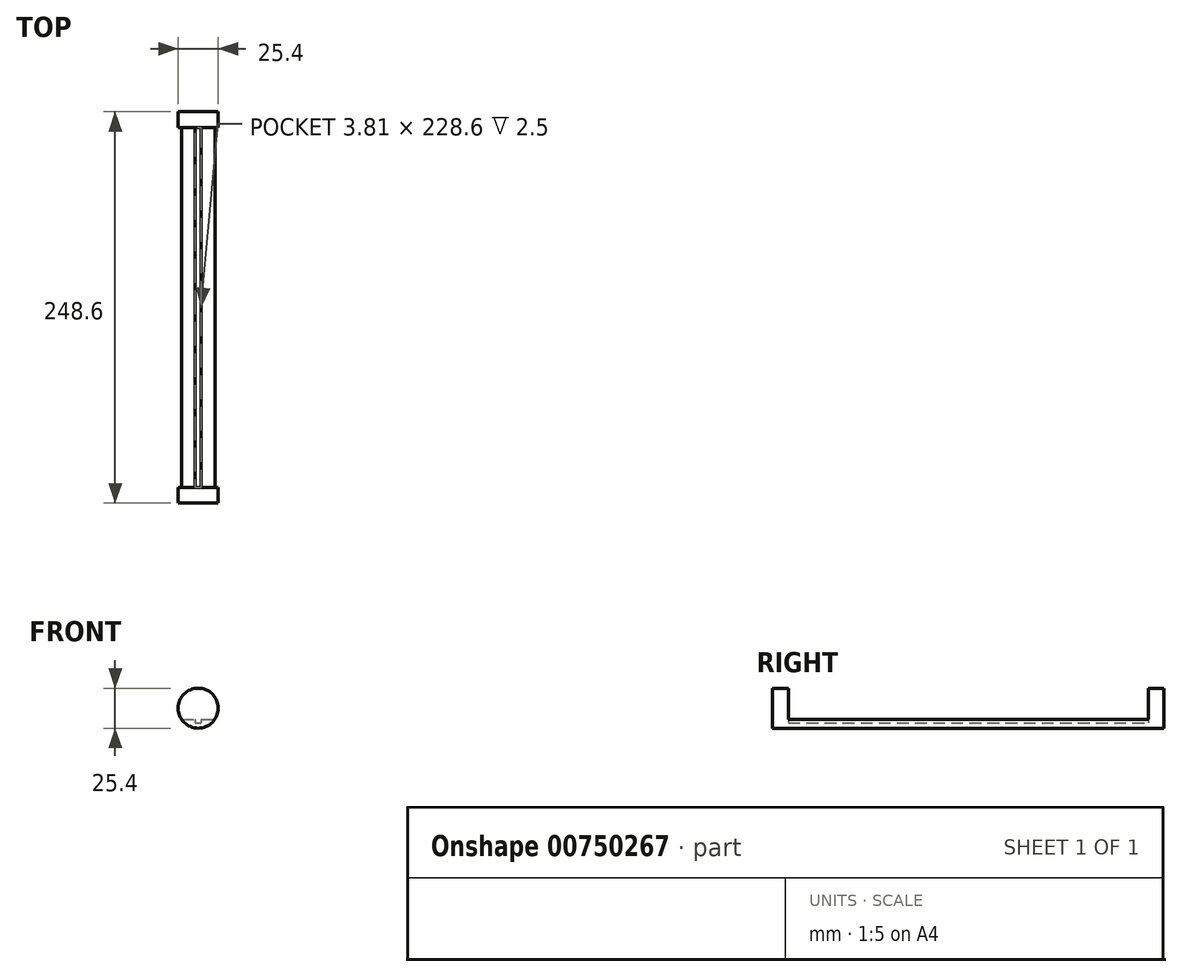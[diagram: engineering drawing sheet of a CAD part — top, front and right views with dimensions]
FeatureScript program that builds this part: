
annotation { "Feature Type Name" : "Feature", "Feature Type Description" : "" }
export const myFeature = defineFeature(function(context is Context, id is Id, definition is map)
    precondition{}
    {
        {
            var Q0;
            Q0=qCreatedBy(makeId("Front.planeOp"),FACE);
            var sketch = newSketch(context, id + "F0", { "sketchPlane" : qUnion([Q0])});
            skArc(sketch, "E0", {"start": v(-10.6, -7) * mm, "mid": v(0, -12.7) * mm, "end": v(10.6, -7) * mm});
            skLineSegment(sketch, "E1", {"start": v(-10.6, -7) * mm, "end": v(10.6, -7) * mm});
            skSolve(sketch);
        }
        {
            var Q0;
            Q0=qSketchRegion(id+"F0",true);
            extrude(context, id + "F1", {"entities" : qUnion([Q0]), "depth" : 114.3 * mm, "offsetDistance" : 25.4 * mm});
        }
        {
            var Q0;
            Q0=makeQuery(id+"F1.opExtrude","CAP_FACE",FACE,{"disambiguationData":[OSD([sQuery(id+"F0.wireOp",EDGE,"E0"),sQuery(id+"F0.wireOp",EDGE,"E1")])],"isStart":false});
            var sketch = newSketch(context, id + "F2", { "sketchPlane" : qUnion([Q0])});
            skCircle(sketch, "E2", {"center": v(0, 0) * mm, "radius": 12.7 * mm});
            skSolve(sketch);
        }
        {
            var Q0;
            Q0=qSketchRegion(id+"F2",true);
            extrude(context, id + "F3", {"entities" : qUnion([Q0]), "operationType" : NewBodyOperationType.ADD, "depth" : 10 * mm, "offsetDistance" : 25.4 * mm});
        }
        {
            var Q0;
            Q0=makeQuery(id+"F1.opExtrude","CAP_FACE",FACE,{"disambiguationData":[OSD([sQuery(id+"F0.wireOp",EDGE,"E0"),sQuery(id+"F0.wireOp",EDGE,"E1")])],"isStart":true});
            var sketch = newSketch(context, id + "F4", { "sketchPlane" : qUnion([Q0])});
            skArc(sketch, "E3", {"start": v(-10.6, -7) * mm, "mid": v(0, -12.7) * mm, "end": v(10.6, -7) * mm});
            skLineSegment(sketch, "E4", {"start": v(-10.6, -7) * mm, "end": v(10.6, -7) * mm});
            skLineSegment(sketch, "E5.top", {"start": v(1.9, -9.5) * mm, "end": v(-1.9, -9.5) * mm});
            skLineSegment(sketch, "E5.left", {"start": v(1.9, -7) * mm, "end": v(1.9, -9.5) * mm});
            skLineSegment(sketch, "E5.right", {"start": v(-1.9, -7) * mm, "end": v(-1.9, -9.5) * mm});
            skSolve(sketch);
        }
        {
            var Q0;
            Q0=makeQuery(id+"F4.imprint","IMPRINT",FACE,{"disambiguationData":[TD([[makeQuery(id+"F4.imprint","IMPRINT",EDGE,{"derivedFrom":sQuery(id+"F4.wireOp",EDGE,"E5.top")}),-1.0]])]});
            extrude(context, id + "F5", {"entities" : qUnion([Q0]), "operationType" : NewBodyOperationType.REMOVE, "oppositeDirection" : true, "depth" : 114.3 * mm, "offsetDistance" : 25.4 * mm});
        }
        {
            var Q0;
            Q0=makeQuery(id+"F1.opExtrude","SWEPT_BODY",BODY,{"disambiguationData":[OSD([sQuery(id+"F0.wireOp",EDGE,"E0"),sQuery(id+"F0.wireOp",EDGE,"E1")])]});
            var Q1;
            Q1=makeQuery(id+"F1.opExtrude","CAP_FACE",FACE,{"disambiguationData":[OSD([sQuery(id+"F0.wireOp",EDGE,"E0"),sQuery(id+"F0.wireOp",EDGE,"E1")])],"isStart":true});
            mirror(context, id + "F6", {"operationType" : NewBodyOperationType.ADD, "entities" : qUnion([Q0]), "mirrorPlane" : qUnion([Q1])});
        }
    });
